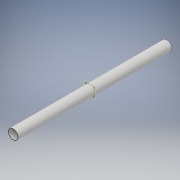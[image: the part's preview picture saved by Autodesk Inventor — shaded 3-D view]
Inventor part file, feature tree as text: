
AUTODESK INVENTOR PART (.ipt)
format: ipt  version: 2017 (Build 210142000, 142)  size: 93,696 bytes
history: native  units: mm
features: extrude x1, sketch x1
ambient origin geometry x8: Origin, YZ Plane, XZ Plane, XY Plane, X Axis, Y Axis, Z Axis, Center Point
bodies: Solid1 (feature_tree)
feature tree (2):
  extrude  "Extrusion1"  Depth=338.0mm
  sketch  "Sketch2"  dims[d0=22.0mm d1=1.0mm d2=338.0mm d3=0.0mm]
